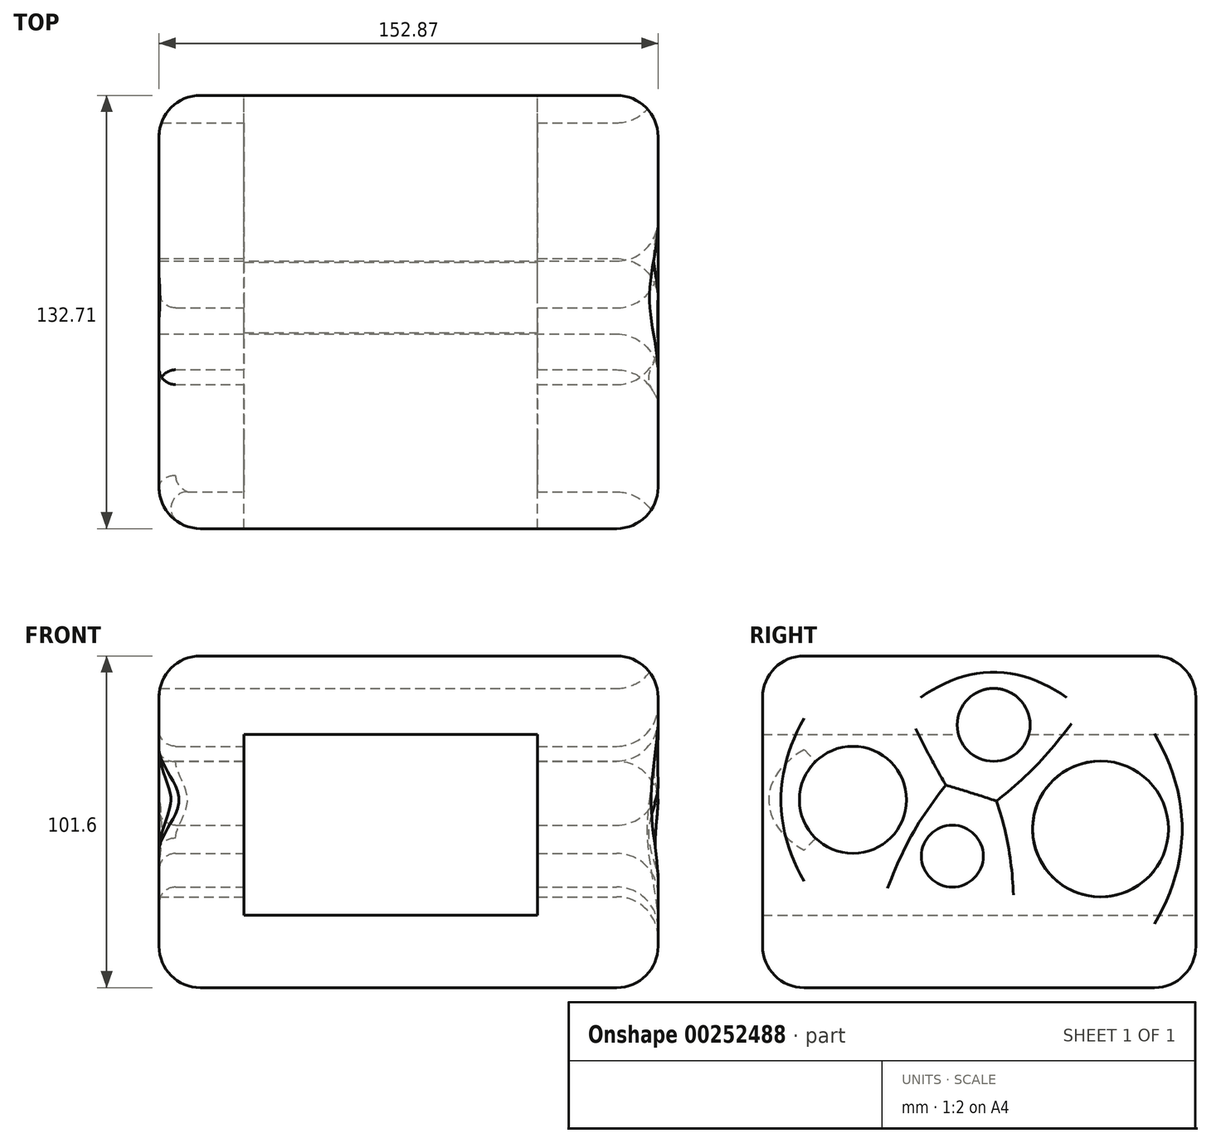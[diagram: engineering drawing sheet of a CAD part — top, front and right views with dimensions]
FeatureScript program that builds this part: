
annotation { "Feature Type Name" : "Feature", "Feature Type Description" : "" }
export const myFeature = defineFeature(function(context is Context, id is Id, definition is map)
    precondition{}
    {
        {
            var Q0;
            Q0=qCreatedBy(makeId("Top.planeOp"),FACE);
            var sketch = newSketch(context, id + "F0", { "sketchPlane" : qUnion([Q0])});
            skLineSegment(sketch, "E0.bottom", {"start": v(76.18, 76.7) * mm, "end": v(-76.7, 76.7) * mm});
            skLineSegment(sketch, "E0.top", {"start": v(76.18, -56.02) * mm, "end": v(-76.7, -56.02) * mm});
            skLineSegment(sketch, "E0.left", {"start": v(76.18, 76.7) * mm, "end": v(76.18, -56.02) * mm});
            skLineSegment(sketch, "E0.right", {"start": v(-76.7, 76.7) * mm, "end": v(-76.7, -56.02) * mm});
            skSolve(sketch);
        }
        {
            var Q0;
            Q0=makeQuery(id+"F0.imprint","IMPRINT",FACE,{"disambiguationData":[TD([[makeQuery(id+"F0.imprint","IMPRINT",EDGE,{"derivedFrom":sQuery(id+"F0.wireOp",EDGE,"E0.bottom")}),1.0]])]});
            extrude(context, id + "F1", {"entities" : qUnion([Q0]), "depth" : 101.6 * mm});
        }
        {
            var Q0;
            Q0=makeQuery(id+"F1.opExtrude","SWEPT_FACE",FACE,{"disambiguationData":[OSD([sQuery(id+"F0.wireOp",EDGE,"E0.left")])]});
            var sketch = newSketch(context, id + "F2", { "sketchPlane" : qUnion([Q0])});
            skCircle(sketch, "E1", {"center": v(14.75, 80.48) * mm, "radius": 11.17 * mm});
            skCircle(sketch, "E2", {"center": v(47.5, 48.6) * mm, "radius": 20.8 * mm});
            skCircle(sketch, "E3", {"center": v(-28.33, 57.5) * mm, "radius": 16.41 * mm});
            skCircle(sketch, "E4", {"center": v(2.11, 40.27) * mm, "radius": 9.48 * mm});
            skSolve(sketch);
        }
        {
            var Q0;
            Q0=makeQuery(id+"F2.imprint","IMPRINT",FACE,{"disambiguationData":[TD([[makeQuery(id+"F2.imprint","IMPRINT",EDGE,{"derivedFrom":sQuery(id+"F2.wireOp",EDGE,"E2")}),1.0]])]});
            var Q1;
            Q1=makeQuery(id+"F2.imprint","IMPRINT",FACE,{"disambiguationData":[TD([[makeQuery(id+"F2.imprint","IMPRINT",EDGE,{"derivedFrom":sQuery(id+"F2.wireOp",EDGE,"E1")}),1.0]])]});
            var Q2;
            Q2=makeQuery(id+"F2.imprint","IMPRINT",FACE,{"disambiguationData":[TD([[makeQuery(id+"F2.imprint","IMPRINT",EDGE,{"derivedFrom":sQuery(id+"F2.wireOp",EDGE,"E4")}),1.0]])]});
            var Q3;
            Q3=makeQuery(id+"F2.imprint","IMPRINT",FACE,{"disambiguationData":[TD([[makeQuery(id+"F2.imprint","IMPRINT",EDGE,{"derivedFrom":sQuery(id+"F2.wireOp",EDGE,"E3")}),1.0]])]});
            extrude(context, id + "F3", {"entities" : qUnion([Q0, Q1, Q2, Q3]), "operationType" : NewBodyOperationType.REMOVE, "oppositeDirection" : true, "depth" : 177.8 * mm});
        }
        {
            var Q0;
            Q0=makeQuery(id+"F1.opExtrude","SWEPT_FACE",FACE,{"disambiguationData":[OSD([sQuery(id+"F0.wireOp",EDGE,"E0.bottom")])]});
            var sketch = newSketch(context, id + "F4", { "sketchPlane" : qUnion([Q0])});
            skLineSegment(sketch, "E5", {"start": v(-39.25, 77.61) * mm, "end": v(-39.25, 22.18) * mm});
            skLineSegment(sketch, "E6", {"start": v(-39.25, 22.18) * mm, "end": v(50.65, 22.18) * mm});
            skLineSegment(sketch, "E7", {"start": v(50.65, 22.18) * mm, "end": v(50.65, 77.61) * mm});
            skLineSegment(sketch, "E8", {"start": v(50.65, 77.61) * mm, "end": v(-39.25, 77.61) * mm});
            skSolve(sketch);
        }
        {
            var Q0;
            Q0=makeQuery(id+"F4.imprint","IMPRINT",FACE,{"disambiguationData":[TD([[makeQuery(id+"F4.imprint","IMPRINT",EDGE,{"derivedFrom":sQuery(id+"F4.wireOp",EDGE,"E5")}),1.0]])]});
            extrude(context, id + "F5", {"entities" : qUnion([Q0]), "operationType" : NewBodyOperationType.REMOVE, "oppositeDirection" : true, "depth" : 152.4 * mm});
        }
        {
            var Q0;
            Q0=makeQuery(id+"F1.opExtrude","CAP_EDGE",EDGE,{"disambiguationData":[OSD([sQuery(id+"F0.wireOp",EDGE,"E0.top")])],"isStart":false});
            var Q1;
            Q1=makeQuery(id+"F1.opExtrude","CAP_EDGE",EDGE,{"disambiguationData":[OSD([sQuery(id+"F0.wireOp",EDGE,"E0.right")])],"isStart":false});
            var Q2;
            Q2=makeQuery(id+"F1.opExtrude","CAP_EDGE",EDGE,{"disambiguationData":[OSD([sQuery(id+"F0.wireOp",EDGE,"E0.bottom")])],"isStart":false});
            var Q3;
            Q3=makeQuery(id+"F1.opExtrude","CAP_EDGE",EDGE,{"disambiguationData":[OSD([sQuery(id+"F0.wireOp",EDGE,"E0.left")])],"isStart":false});
            var Q4;
            Q4=makeQuery(id+"F1.opExtrude","SWEPT_EDGE",EDGE,{"disambiguationData":[OSD([sQuery(id+"F0.wireOp",EDGE,"E0.top"),sQuery(id+"F0.wireOp",EDGE,"E0.left")])]});
            var Q5;
            Q5=makeQuery(id+"F1.opExtrude","SWEPT_EDGE",EDGE,{"disambiguationData":[OSD([sQuery(id+"F0.wireOp",EDGE,"E0.top"),sQuery(id+"F0.wireOp",EDGE,"E0.right")])]});
            var Q6;
            Q6=makeQuery(id+"F1.opExtrude","CAP_EDGE",EDGE,{"disambiguationData":[OSD([sQuery(id+"F0.wireOp",EDGE,"E0.top")])],"isStart":true});
            var Q7;
            Q7=makeQuery(id+"F1.opExtrude","SWEPT_FACE",FACE,{"disambiguationData":[OSD([sQuery(id+"F0.wireOp",EDGE,"E0.left")])]});
            var Q8;
            Q8=makeQuery(id+"F1.opExtrude","SWEPT_EDGE",EDGE,{"disambiguationData":[OSD([sQuery(id+"F0.wireOp",EDGE,"E0.bottom"),sQuery(id+"F0.wireOp",EDGE,"E0.left")])]});
            var Q9;
            Q9=makeQuery(id+"F1.opExtrude","CAP_EDGE",EDGE,{"disambiguationData":[OSD([sQuery(id+"F0.wireOp",EDGE,"E0.bottom")])],"isStart":true});
            var Q10;
            Q10=makeQuery(id+"F1.opExtrude","CAP_EDGE",EDGE,{"disambiguationData":[OSD([sQuery(id+"F0.wireOp",EDGE,"E0.right")])],"isStart":true});
            var Q11;
            Q11=makeQuery(id+"F1.opExtrude","SWEPT_EDGE",EDGE,{"disambiguationData":[OSD([sQuery(id+"F0.wireOp",EDGE,"E0.bottom"),sQuery(id+"F0.wireOp",EDGE,"E0.right")])]});
            fillet(context, id + "F6", {"entities" : qUnion([Q0, Q1, Q2, Q3, Q4, Q5, Q6, Q7, Q8, Q9, Q10, Q11]), "radius" : 12.7 * mm, "tangentPropagation" : true, "allowEdgeOverflow" : false});
        }
        {
            var Q0;
            Q0=makeQuery(id+"F3.boolean.opBoolean","INTERSECT",EDGE,{"derivedFrom":[makeQuery(id+"F1.opExtrude","SWEPT_FACE",FACE,{"disambiguationData":[OSD([sQuery(id+"F0.wireOp",EDGE,"E0.right")])]}),makeQuery(id+"F3.opExtrude","SWEPT_FACE",FACE,{"disambiguationData":[OSD([sQuery(id+"F2.wireOp",EDGE,"E4")])]})]});
            var Q1;
            Q1=makeQuery(id+"F3.boolean.opBoolean","INTERSECT",EDGE,{"derivedFrom":[makeQuery(id+"F1.opExtrude","SWEPT_FACE",FACE,{"disambiguationData":[OSD([sQuery(id+"F0.wireOp",EDGE,"E0.right")])]}),makeQuery(id+"F3.opExtrude","SWEPT_FACE",FACE,{"disambiguationData":[OSD([sQuery(id+"F2.wireOp",EDGE,"E3")])]})]});
            fillet(context, id + "F7", {"entities" : qUnion([Q0, Q1]), "radius" : 5.08 * mm, "tangentPropagation" : true, "allowEdgeOverflow" : false});
        }
    });
